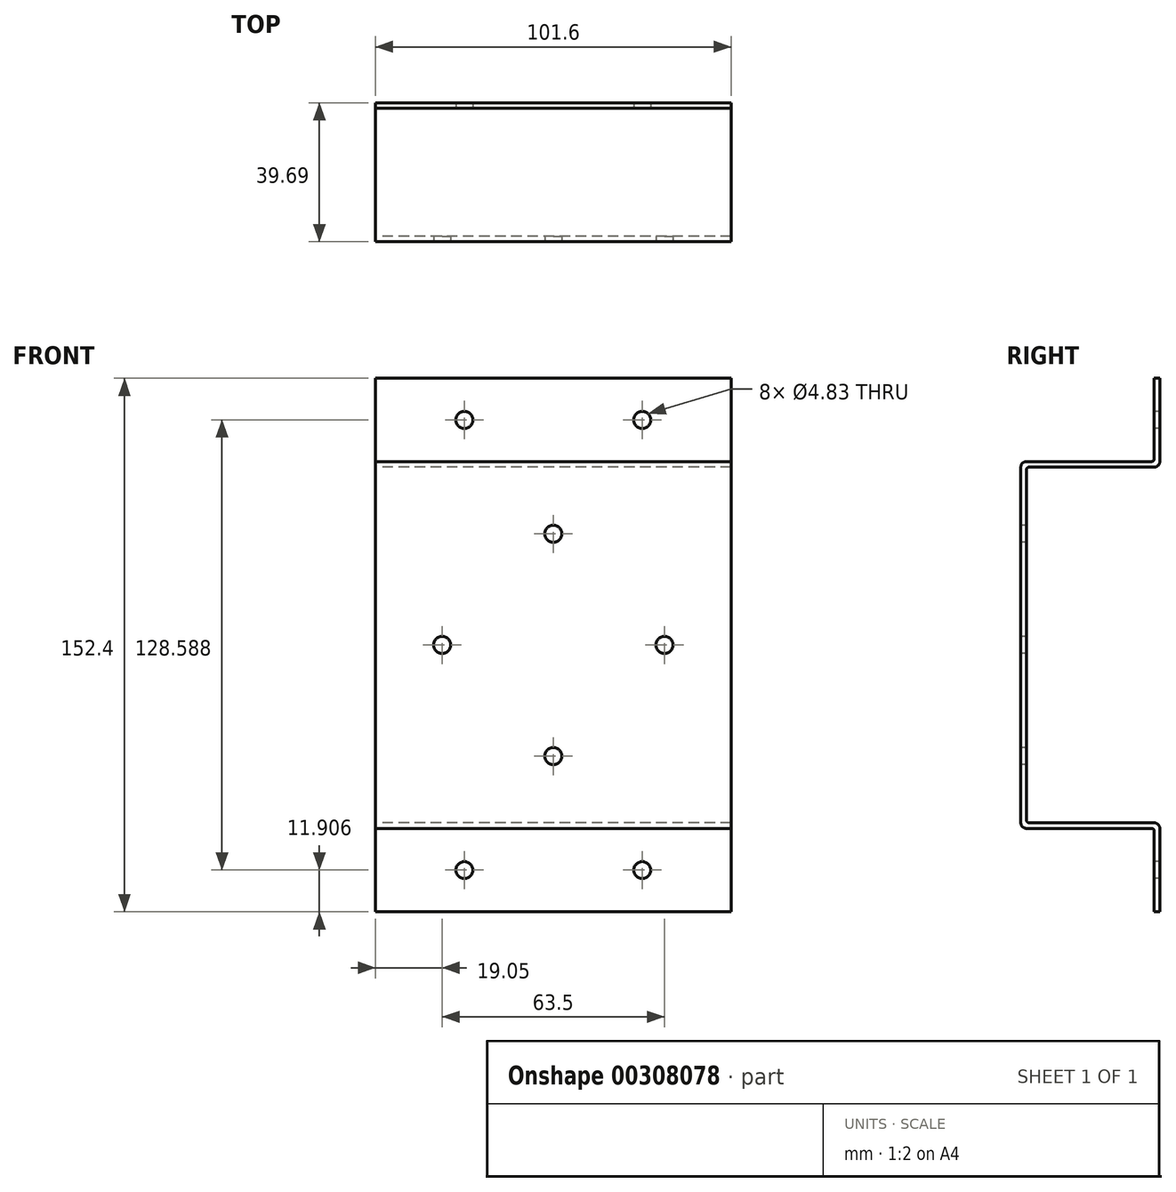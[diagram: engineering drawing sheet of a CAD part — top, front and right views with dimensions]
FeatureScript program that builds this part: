
annotation { "Feature Type Name" : "Feature", "Feature Type Description" : "" }
export const myFeature = defineFeature(function(context is Context, id is Id, definition is map)
    precondition{}
    {
        {
            var Q0;
            Q0=qCreatedBy(makeId("Right.planeOp"),FACE);
            var sketch = newSketch(context, id + "F0", { "sketchPlane" : qUnion([Q0])});
            skLineSegment(sketch, "E0", {"start": v(-1.59, 50.8) * mm, "end": v(-37.3, 50.8) * mm});
            skLineSegment(sketch, "E1", {"start": v(-38.1, 50) * mm, "end": v(-38.1, 0) * mm});
            skLineSegment(sketch, "E2", {"start": v(-38.1, 0) * mm, "end": v(-38.1, -50) * mm});
            skLineSegment(sketch, "E3", {"start": v(-37.3, -50.8) * mm, "end": v(-1.59, -50.8) * mm});
            skLineSegment(sketch, "E4", {"start": v(0, -52.39) * mm, "end": v(0, -76.2) * mm});
            skLineSegment(sketch, "E5", {"start": v(0, 52.39) * mm, "end": v(0, 76.2) * mm});
            skLineSegment(sketch, "E6.0", {"start": v(-1.59, -53.18) * mm, "end": v(-1.59, -76.2) * mm});
            skLineSegment(sketch, "E7.0", {"start": v(-38.1, -52.39) * mm, "end": v(-2.38, -52.39) * mm});
            skLineSegment(sketch, "E8.0", {"start": v(-39.69, 0) * mm, "end": v(-39.69, -50.8) * mm});
            skLineSegment(sketch, "E9.0", {"start": v(-39.69, 50.8) * mm, "end": v(-39.69, 0) * mm});
            skLineSegment(sketch, "E10.0", {"start": v(-2.38, 52.39) * mm, "end": v(-38.1, 52.39) * mm});
            skLineSegment(sketch, "E11.0", {"start": v(-1.59, 53.18) * mm, "end": v(-1.59, 76.2) * mm});
            skLineSegment(sketch, "E12", {"start": v(-1.59, -76.2) * mm, "end": v(0, -76.2) * mm});
            skLineSegment(sketch, "E13", {"start": v(0, 76.2) * mm, "end": v(-1.59, 76.2) * mm});
            skPoint(sketch, "E14.visualSharp", {"position": v(-38.1, -50.8) * mm});
            skPoint(sketch, "E15.visualSharp", {"position": v(-39.69, -52.39) * mm});
            skArc(sketch, "E16.filletArc", {"start": v(-38.1, -50) * mm, "mid": v(-37.87, -50.57) * mm, "end": v(-37.3, -50.8) * mm});
            skPoint(sketch, "E17.visualSharp", {"position": v(-38.1, 50.8) * mm});
            skArc(sketch, "E17.filletArc", {"start": v(-37.3, 50.8) * mm, "mid": v(-37.87, 50.57) * mm, "end": v(-38.1, 50) * mm});
            skPoint(sketch, "E18.visualSharp", {"position": v(-39.69, 52.39) * mm});
            skArc(sketch, "E18.filletArc", {"start": v(-38.1, 52.39) * mm, "mid": v(-39.22, 51.92) * mm, "end": v(-39.69, 50.8) * mm});
            skArc(sketch, "E19.filletArc", {"start": v(-39.69, -50.8) * mm, "mid": v(-39.22, -51.92) * mm, "end": v(-38.1, -52.39) * mm});
            skPoint(sketch, "E20.visualSharp", {"position": v(0, -50.8) * mm});
            skArc(sketch, "E20.filletArc", {"start": v(0, -52.39) * mm, "mid": v(-0.46, -51.26) * mm, "end": v(-1.59, -50.8) * mm});
            skPoint(sketch, "E21.visualSharp", {"position": v(0, 50.8) * mm});
            skArc(sketch, "E21.filletArc", {"start": v(-1.59, 50.8) * mm, "mid": v(-0.46, 51.26) * mm, "end": v(0, 52.39) * mm});
            skArc(sketch, "E22.filletArc", {"start": v(-2.38, 52.39) * mm, "mid": v(-1.82, 52.62) * mm, "end": v(-1.59, 53.18) * mm});
            skArc(sketch, "E23.filletArc", {"start": v(-1.59, -53.18) * mm, "mid": v(-1.82, -52.62) * mm, "end": v(-2.38, -52.39) * mm});
            skSolve(sketch);
        }
        {
            var Q0;
            Q0=makeQuery(id+"F0.imprint","IMPRINT",FACE,{"disambiguationData":[TD([[makeQuery(id+"F0.imprint","IMPRINT",EDGE,{"derivedFrom":sQuery(id+"F0.wireOp",EDGE,"E0")}),-1.0]])]});
            extrude(context, id + "F1", {"entities" : qUnion([Q0]), "depth" : 101.6 * mm, "offsetDistance" : 25.4 * mm});
        }
        {
            var Q0;
            Q0=makeQuery(id+"F1.opExtrude","SWEPT_FACE",FACE,{"disambiguationData":[OSD([sQuery(id+"F0.wireOp",EDGE,"E6.0")])]});
            var sketch = newSketch(context, id + "F2", { "sketchPlane" : qUnion([Q0])});
            skLineSegment(sketch, "E24", {"start": v(0, -64.7) * mm, "end": v(101.6, -64.7) * mm});
            skLineSegment(sketch, "E25", {"start": v(101.6, -76.2) * mm, "end": v(101.6, -53.18) * mm});
            skLineSegment(sketch, "E26.0", {"start": v(76.2, -76.2) * mm, "end": v(76.2, -52.39) * mm});
            skLineSegment(sketch, "E27.0", {"start": v(25.4, -52.39) * mm, "end": v(25.4, -76.2) * mm});
            skPoint(sketch, "E28", {"position": v(25.4, -64.3) * mm});
            skPoint(sketch, "E29", {"position": v(76.2, -64.3) * mm});
            skSolve(sketch);
        }
        {
            var Q0;
            Q0=sQuery(id+"F2.wireOp",VERTEX,"E28");
            var Q1;
            Q1=sQuery(id+"F2.wireOp",VERTEX,"E29");
            var Q2;
            Q2=makeQuery(id+"F1.opExtrude","SWEPT_BODY",BODY,{"disambiguationData":[OSD([sQuery(id+"F0.wireOp",EDGE,"E0"),sQuery(id+"F0.wireOp",EDGE,"E1"),sQuery(id+"F0.wireOp",EDGE,"E2"),sQuery(id+"F0.wireOp",EDGE,"E3"),sQuery(id+"F0.wireOp",EDGE,"E4"),sQuery(id+"F0.wireOp",EDGE,"E5"),sQuery(id+"F0.wireOp",EDGE,"E6.0"),sQuery(id+"F0.wireOp",EDGE,"E7.0"),sQuery(id+"F0.wireOp",EDGE,"E8.0"),sQuery(id+"F0.wireOp",EDGE,"E9.0"),sQuery(id+"F0.wireOp",EDGE,"E10.0"),sQuery(id+"F0.wireOp",EDGE,"E11.0"),sQuery(id+"F0.wireOp",EDGE,"E12"),sQuery(id+"F0.wireOp",EDGE,"E13")])]});
            hole(context, id + "F3", {"style" : HoleStyle.SIMPLE, "endStyle" : HoleEndStyle.THROUGH, "holeDiameter" : 4.83 * mm, "majorDiameter" : 6.35 * mm, "isTappedThrough" : true, "tappedDepth" : 12.7 * mm, "tapClearance" : 3, "startFromSketch" : true, "locations" : qUnion([Q0, Q1]), "scope" : qUnion([Q2])});
        }
        {
            var Q0;
            Q0=makeQuery(id+"F1.opExtrude","SWEPT_FACE",FACE,{"disambiguationData":[OSD([sQuery(id+"F0.wireOp",EDGE,"E11.0")])]});
            var sketch = newSketch(context, id + "F4", { "sketchPlane" : qUnion([Q0])});
            skLineSegment(sketch, "E30", {"start": v(0, 64.7) * mm, "end": v(101.6, 64.7) * mm});
            skPoint(sketch, "E30.endSnap0", {"position": v(0, 64.7) * mm});
            skLineSegment(sketch, "E31.0", {"start": v(25.4, 52.39) * mm, "end": v(25.4, 76.2) * mm});
            skLineSegment(sketch, "E32.0", {"start": v(76.2, 52.39) * mm, "end": v(76.2, 76.2) * mm});
            skPoint(sketch, "E33", {"position": v(25.4, 64.3) * mm});
            skPoint(sketch, "E34", {"position": v(76.2, 64.3) * mm});
            skSolve(sketch);
        }
        {
            var Q0;
            Q0=sQuery(id+"F4.wireOp",VERTEX,"E33");
            var Q1;
            Q1=sQuery(id+"F4.wireOp",VERTEX,"E34");
            var Q2;
            Q2=makeQuery(id+"F1.opExtrude","SWEPT_BODY",BODY,{"disambiguationData":[OSD([sQuery(id+"F0.wireOp",EDGE,"E0"),sQuery(id+"F0.wireOp",EDGE,"E1"),sQuery(id+"F0.wireOp",EDGE,"E2"),sQuery(id+"F0.wireOp",EDGE,"E3"),sQuery(id+"F0.wireOp",EDGE,"E4"),sQuery(id+"F0.wireOp",EDGE,"E5"),sQuery(id+"F0.wireOp",EDGE,"E6.0"),sQuery(id+"F0.wireOp",EDGE,"E7.0"),sQuery(id+"F0.wireOp",EDGE,"E8.0"),sQuery(id+"F0.wireOp",EDGE,"E9.0"),sQuery(id+"F0.wireOp",EDGE,"E10.0"),sQuery(id+"F0.wireOp",EDGE,"E11.0"),sQuery(id+"F0.wireOp",EDGE,"E12"),sQuery(id+"F0.wireOp",EDGE,"E13")])]});
            hole(context, id + "F5", {"style" : HoleStyle.SIMPLE, "endStyle" : HoleEndStyle.THROUGH, "holeDiameter" : 4.83 * mm, "majorDiameter" : 6.35 * mm, "isTappedThrough" : true, "tappedDepth" : 12.7 * mm, "tapClearance" : 3, "startFromSketch" : true, "locations" : qUnion([Q0, Q1]), "scope" : qUnion([Q2])});
        }
        {
            var Q0;
            Q0=makeQuery(id+"F1.opExtrude","SWEPT_FACE",FACE,{"disambiguationData":[OSD([sQuery(id+"F0.wireOp",EDGE,"E8.0"),sQuery(id+"F0.wireOp",EDGE,"E9.0")])]});
            var sketch = newSketch(context, id + "F6", { "sketchPlane" : qUnion([Q0])});
            skLineSegment(sketch, "E35", {"start": v(0, 0) * mm, "end": v(101.6, 0) * mm});
            skLineSegment(sketch, "E36.0", {"start": v(82.55, 52.39) * mm, "end": v(82.55, -52.39) * mm});
            skLineSegment(sketch, "E37.0", {"start": v(19.05, 52.39) * mm, "end": v(19.05, -52.39) * mm});
            skPoint(sketch, "E38", {"position": v(19.05, 0) * mm});
            skPoint(sketch, "E39", {"position": v(82.55, 0) * mm});
            skSolve(sketch);
        }
        {
            var Q0;
            Q0=sQuery(id+"F6.wireOp",VERTEX,"E38");
            var Q1;
            Q1=sQuery(id+"F6.wireOp",VERTEX,"E39");
            var Q2;
            Q2=makeQuery(id+"F1.opExtrude","SWEPT_BODY",BODY,{"disambiguationData":[OSD([sQuery(id+"F0.wireOp",EDGE,"E0"),sQuery(id+"F0.wireOp",EDGE,"E1"),sQuery(id+"F0.wireOp",EDGE,"E2"),sQuery(id+"F0.wireOp",EDGE,"E3"),sQuery(id+"F0.wireOp",EDGE,"E4"),sQuery(id+"F0.wireOp",EDGE,"E5"),sQuery(id+"F0.wireOp",EDGE,"E6.0"),sQuery(id+"F0.wireOp",EDGE,"E7.0"),sQuery(id+"F0.wireOp",EDGE,"E8.0"),sQuery(id+"F0.wireOp",EDGE,"E9.0"),sQuery(id+"F0.wireOp",EDGE,"E10.0"),sQuery(id+"F0.wireOp",EDGE,"E11.0"),sQuery(id+"F0.wireOp",EDGE,"E12"),sQuery(id+"F0.wireOp",EDGE,"E13")])]});
            hole(context, id + "F7", {"style" : HoleStyle.SIMPLE, "endStyle" : HoleEndStyle.THROUGH, "holeDiameter" : 4.83 * mm, "majorDiameter" : 6.35 * mm, "isTappedThrough" : true, "tappedDepth" : 12.7 * mm, "tapClearance" : 3, "startFromSketch" : true, "locations" : qUnion([Q0, Q1]), "scope" : qUnion([Q2])});
        }
        {
            var Q0;
            Q0=makeQuery(id+"F1.opExtrude","SWEPT_FACE",FACE,{"disambiguationData":[OSD([sQuery(id+"F0.wireOp",EDGE,"E8.0"),sQuery(id+"F0.wireOp",EDGE,"E9.0")])]});
            var sketch = newSketch(context, id + "F8", { "sketchPlane" : qUnion([Q0])});
            skLineSegment(sketch, "E40", {"start": v(19.05, 0) * mm, "end": v(82.55, 0) * mm});
            skLineSegment(sketch, "E41", {"start": v(50.8, -50.8) * mm, "end": v(50.8, 50.8) * mm});
            skLineSegment(sketch, "E42.0", {"start": v(19.05, -31.75) * mm, "end": v(82.55, -31.75) * mm});
            skLineSegment(sketch, "E43.0", {"start": v(19.05, 31.75) * mm, "end": v(82.55, 31.75) * mm});
            skPoint(sketch, "E44", {"position": v(50.8, -31.75) * mm});
            skPoint(sketch, "E45", {"position": v(50.8, 31.75) * mm});
            skSolve(sketch);
        }
        {
            var Q0;
            Q0=sQuery(id+"F8.wireOp",VERTEX,"E44");
            var Q1;
            Q1=sQuery(id+"F8.wireOp",VERTEX,"E45");
            var Q2;
            Q2=makeQuery(id+"F1.opExtrude","SWEPT_BODY",BODY,{"disambiguationData":[OSD([sQuery(id+"F0.wireOp",EDGE,"E0"),sQuery(id+"F0.wireOp",EDGE,"E1"),sQuery(id+"F0.wireOp",EDGE,"E2"),sQuery(id+"F0.wireOp",EDGE,"E3"),sQuery(id+"F0.wireOp",EDGE,"E4"),sQuery(id+"F0.wireOp",EDGE,"E5"),sQuery(id+"F0.wireOp",EDGE,"E6.0"),sQuery(id+"F0.wireOp",EDGE,"E7.0"),sQuery(id+"F0.wireOp",EDGE,"E8.0"),sQuery(id+"F0.wireOp",EDGE,"E9.0"),sQuery(id+"F0.wireOp",EDGE,"E10.0"),sQuery(id+"F0.wireOp",EDGE,"E11.0"),sQuery(id+"F0.wireOp",EDGE,"E12"),sQuery(id+"F0.wireOp",EDGE,"E13"),sQuery(id+"F0.wireOp",EDGE,"E16.filletArc"),sQuery(id+"F0.wireOp",EDGE,"E17.filletArc"),sQuery(id+"F0.wireOp",EDGE,"E18.filletArc"),sQuery(id+"F0.wireOp",EDGE,"E19.filletArc"),sQuery(id+"F0.wireOp",EDGE,"E20.filletArc"),sQuery(id+"F0.wireOp",EDGE,"E21.filletArc"),sQuery(id+"F0.wireOp",EDGE,"E22.filletArc"),sQuery(id+"F0.wireOp",EDGE,"E23.filletArc")])]});
            hole(context, id + "F9", {"style" : HoleStyle.SIMPLE, "endStyle" : HoleEndStyle.THROUGH, "holeDiameter" : 4.83 * mm, "majorDiameter" : 6.35 * mm, "isTappedThrough" : true, "tappedDepth" : 12.7 * mm, "tapClearance" : 3, "startFromSketch" : true, "locations" : qUnion([Q0, Q1]), "scope" : qUnion([Q2])});
        }
    });
